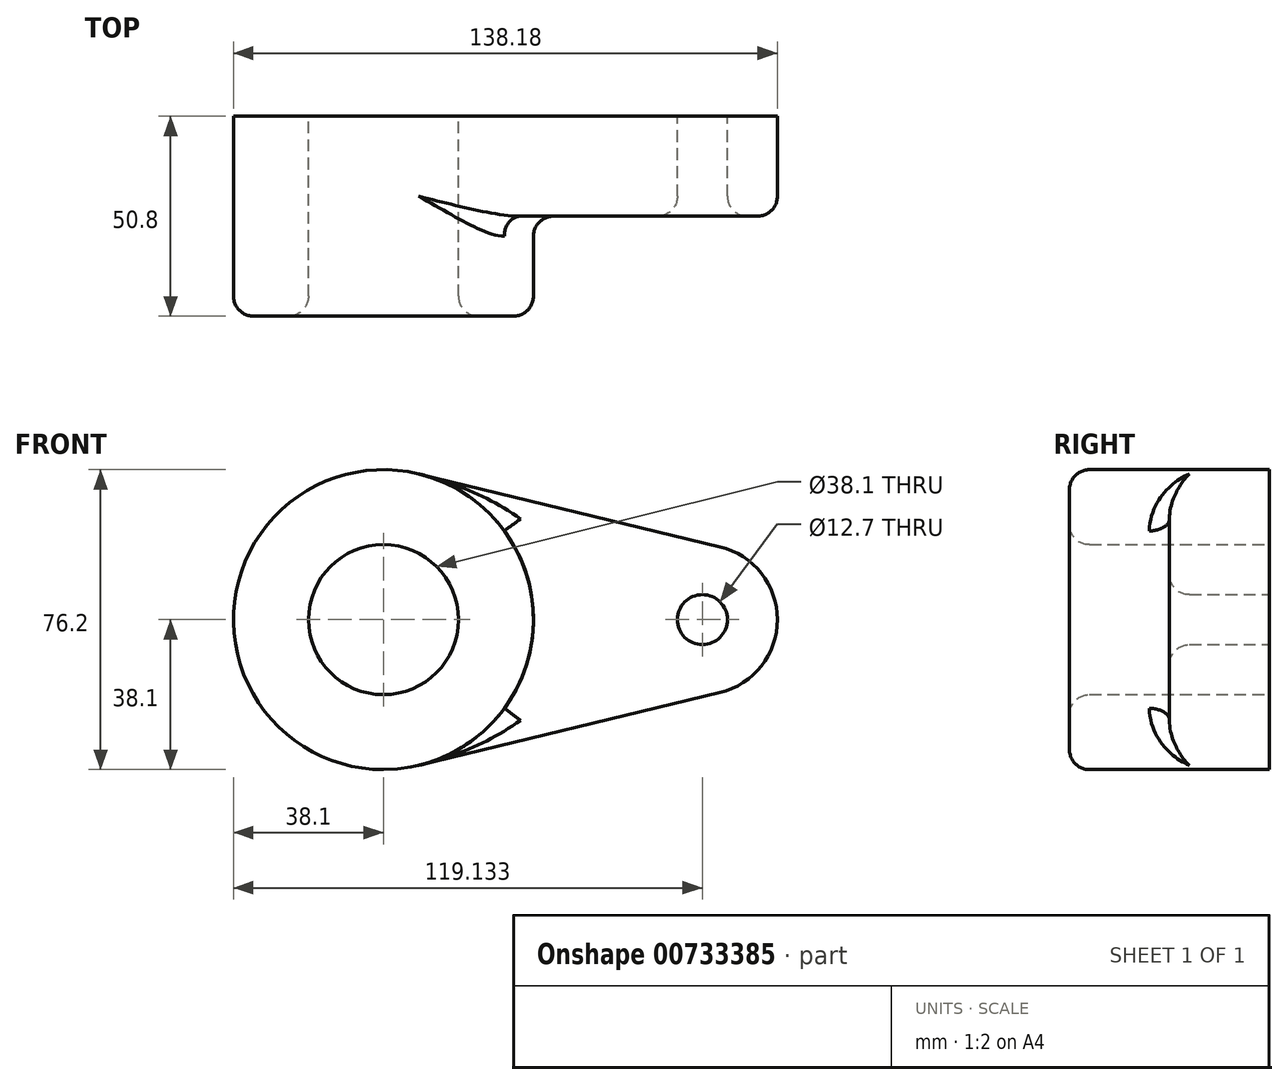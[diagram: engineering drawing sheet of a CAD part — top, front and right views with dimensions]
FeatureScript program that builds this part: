
annotation { "Feature Type Name" : "Feature", "Feature Type Description" : "" }
export const myFeature = defineFeature(function(context is Context, id is Id, definition is map)
    precondition{}
    {
        {
            var Q0;
            Q0=qCreatedBy(makeId("Front.planeOp"),FACE);
            var sketch = newSketch(context, id + "F0", { "sketchPlane" : qUnion([Q0])});
            skCircle(sketch, "E0", {"center": v(0, 0) * mm, "radius": 38.1 * mm});
            skCircle(sketch, "E1", {"center": v(81.03, 0) * mm, "radius": 19.05 * mm});
            skCircle(sketch, "E2", {"center": v(0, 0) * mm, "radius": 19.05 * mm});
            skCircle(sketch, "E3", {"center": v(81.03, 0) * mm, "radius": 6.35 * mm});
            skLineSegment(sketch, "E4", {"start": v(8.96, 37.03) * mm, "end": v(85.51, 18.52) * mm});
            skLineSegment(sketch, "E5", {"start": v(85.51, -18.52) * mm, "end": v(8.96, -37.03) * mm});
            skSolve(sketch);
        }
        {
            var Q0;
            Q0 = qSketchRegion(id + "F0", true);
            extrude(context, id + "F1", {"entities" : qUnion([Q0]), "depth" : 25.4 * mm, "offsetDistance" : 25.4 * mm});
        }
        {
            var Q0;
            Q0=makeQuery(id+"F0.imprint","IMPRINT",FACE,{"disambiguationData":[TD([[makeQuery(id+"F0.imprint","IMPRINT",EDGE,{"derivedFrom":sQuery(id+"F0.wireOp",EDGE,"E2")}),-1.0]])]});
            extrude(context, id + "F2", {"entities" : qUnion([Q0]), "operationType" : NewBodyOperationType.ADD, "depth" : 50.8 * mm, "offsetDistance" : 25.4 * mm});
        }
        {
            var Q0;
            Q0=makeQuery(id+"F2.opExtrude","CAP_EDGE",EDGE,{"disambiguationData":[OSD([sQuery(id+"F0.wireOp",EDGE,"E0")])],"isStart":false});
            var Q1;
            Q1=makeQuery(id+"F2.opExtrude","CAP_EDGE",EDGE,{"disambiguationData":[OSD([sQuery(id+"F0.wireOp",EDGE,"E2")])],"isStart":false});
            var Q2;
            Q2=makeQuery(id+"F1.opExtrude","CAP_EDGE",EDGE,{"disambiguationData":[OSD([sQuery(id+"F0.wireOp",EDGE,"E4")])],"isStart":false});
            var Q3;
            Q3=makeQuery(id+"F1.opExtrude","CAP_EDGE",EDGE,{"disambiguationData":[OSD([sQuery(id+"F0.wireOp",EDGE,"E1")])],"isStart":false});
            var Q4;
            Q4=makeQuery(id+"F1.opExtrude","CAP_EDGE",EDGE,{"disambiguationData":[OSD([sQuery(id+"F0.wireOp",EDGE,"E5")])],"isStart":false});
            var Q5;
            Q5=makeQuery(id+"F1.opExtrude","CAP_EDGE",EDGE,{"disambiguationData":[OSD([sQuery(id+"F0.wireOp",EDGE,"E3")])],"isStart":false});
            fillet(context, id + "F3", {"entities" : qUnion([Q0, Q1, Q2, Q3, Q4, Q5]), "radius" : 5.08 * mm, "tangentPropagation" : true, "allowEdgeOverflow" : false});
        }
        {
            var Q0;
            {var subQ0=sQuery(id+"F0.wireOp",EDGE,"E0");Q0=makeQuery(id+"F3.opFillet","BLEND_EDGE",EDGE,{"blendedFrom":[makeQuery(id+"F1.opExtrude","CAP_EDGE",EDGE,{"disambiguationData":[OSD([sQuery(id+"F0.wireOp",EDGE,"E5")])],"isStart":false}),makeQuery(id+"F2.boolean.opBoolean","MERGE",FACE,{"derivedFrom":[makeQuery(id+"F1.opExtrude","SWEPT_FACE",FACE,{"disambiguationData":[OSD([subQ0])]}),makeQuery(id+"F2.opExtrude","SWEPT_FACE",FACE,{"disambiguationData":[OSD([subQ0])]})]})],"blendedInto":[makeQuery(id+"F2.boolean.opBoolean","MERGE",FACE,{"derivedFrom":[makeQuery(id+"F1.opExtrude","SWEPT_FACE",FACE,{"disambiguationData":[OSD([subQ0])]}),makeQuery(id+"F2.opExtrude","SWEPT_FACE",FACE,{"disambiguationData":[OSD([subQ0])]})]})]});}
            fillet(context, id + "F4", {"entities" : qUnion([Q0]), "radius" : 5.08 * mm, "tangentPropagation" : true, "allowEdgeOverflow" : false});
        }
    });
